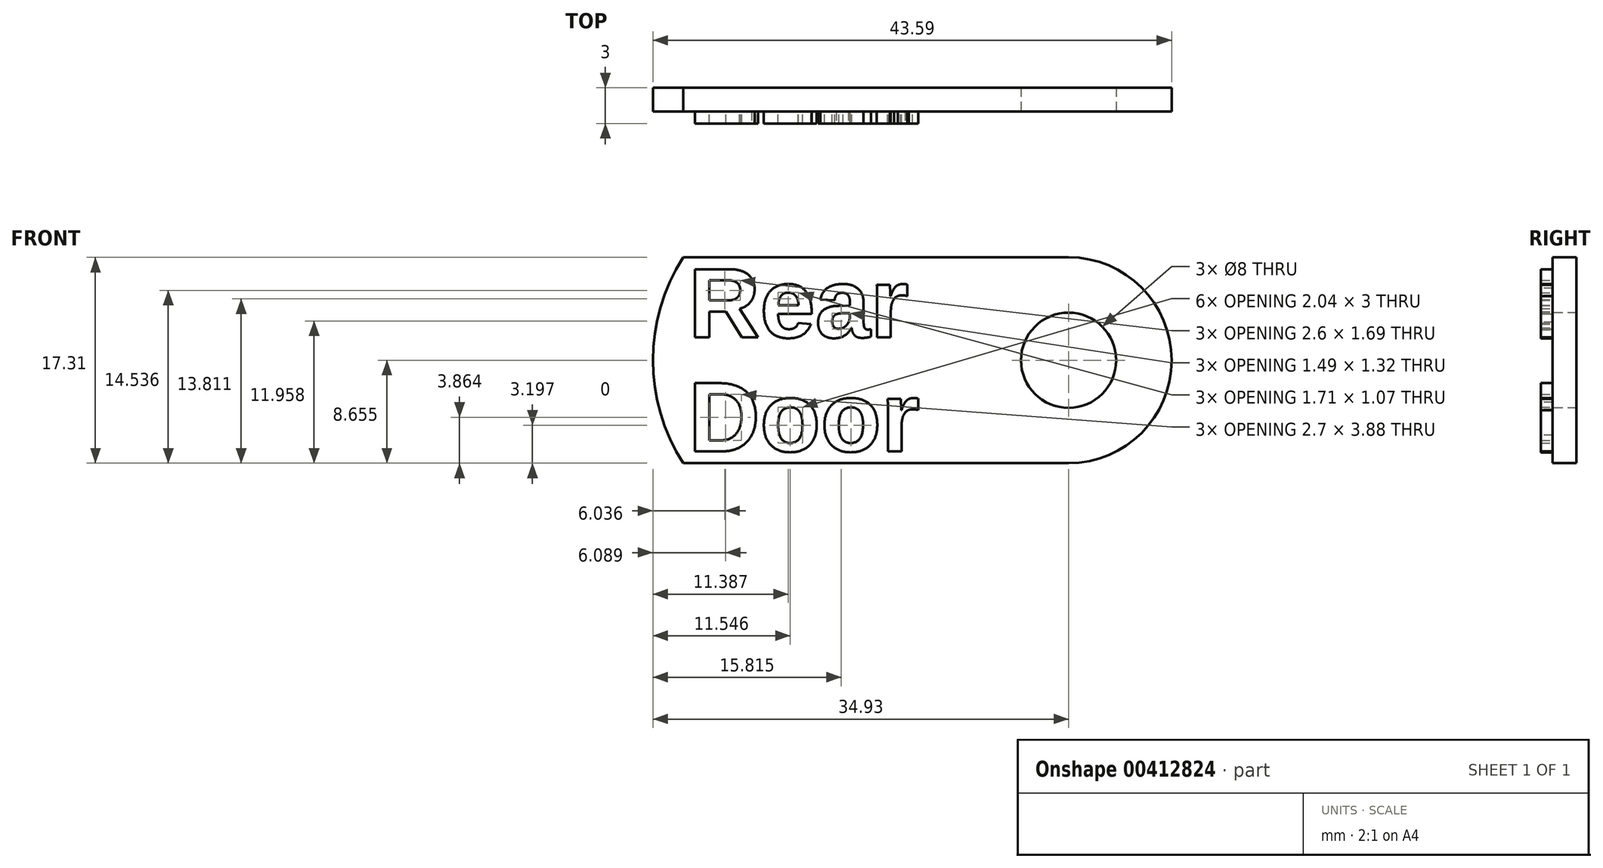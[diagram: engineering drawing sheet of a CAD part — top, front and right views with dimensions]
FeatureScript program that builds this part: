
annotation { "Feature Type Name" : "Feature", "Feature Type Description" : "" }
export const myFeature = defineFeature(function(context is Context, id is Id, definition is map)
    precondition{}
    {
        {
            var Q0;
            Q0=qCreatedBy(makeId("Front.planeOp"),FACE);
            var sketch = newSketch(context, id + "F0", { "sketchPlane" : qUnion([Q0])});
            skText(sketch, "E0", { "text": "Rear \nDoor\n", "fontName": "Arimo-Bold.ttf"});
            const initialGuessF0  = {"E0": [-0.00995, 0, 1, 0, 0.006]};
            skSetInitialGuess(sketch, initialGuessF0);
            skSolve(sketch);
        }
        {
            var Q0;
            Q0=qSketchRegion(id+"F0",true);
            extrude(context, id + "F1", {"entities" : qUnion([Q0]), "depth" : 1 * mm});
        }
        {
            var Q0;
            Q0=qCreatedBy(makeId("Front.planeOp"),FACE);
            var sketch = newSketch(context, id + "F2", { "sketchPlane" : qUnion([Q0])});
            skCircle(sketch, "E1", {"center": v(22, -1.93) * mm, "radius": 4 * mm});
            skArc(sketch, "E2", {"start": v(22, 6.73) * mm, "mid": v(30.66, -1.93) * mm, "end": v(22, -10.58) * mm});
            skLineSegment(sketch, "E3", {"start": v(-10.39, -10.58) * mm, "end": v(22, -10.58) * mm});
            skLineSegment(sketch, "E4", {"start": v(-10.39, 6.73) * mm, "end": v(22, 6.73) * mm});
            skArc(sketch, "E5", {"start": v(-10.39, -10.58) * mm, "mid": v(-12.93, -1.93) * mm, "end": v(-10.39, 6.73) * mm});
            skSolve(sketch);
        }
        {
            var Q0;
            Q0=qSketchRegion(id+"F2",true);
            extrude(context, id + "F3", {"entities" : qUnion([Q0]), "oppositeDirection" : true, "depth" : 2 * mm});
        }
    });
